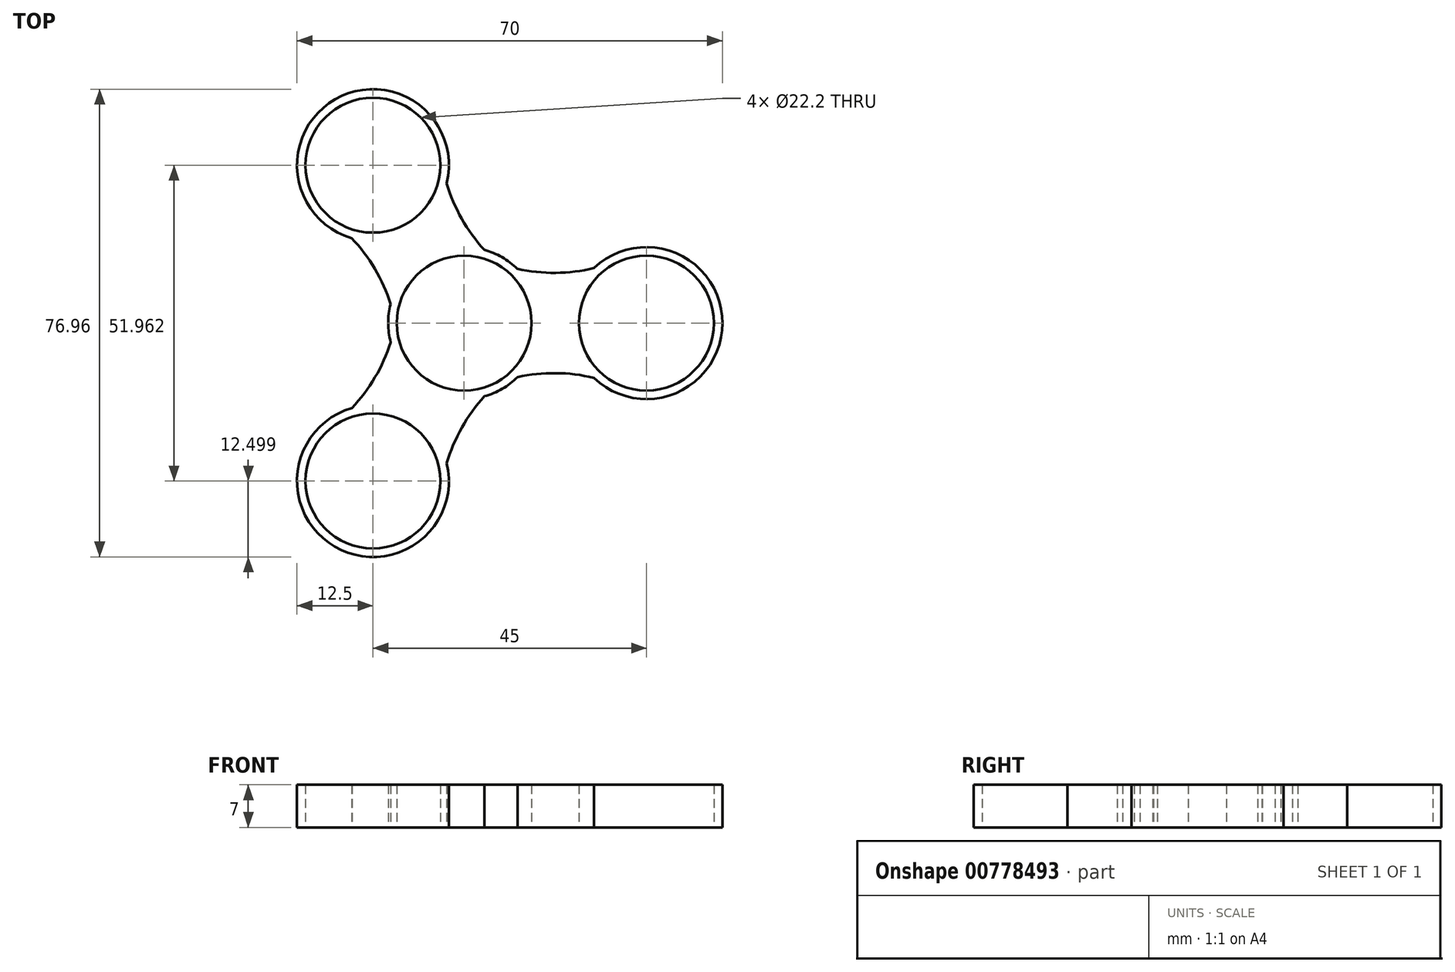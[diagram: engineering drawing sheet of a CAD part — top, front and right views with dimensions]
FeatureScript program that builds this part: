
annotation { "Feature Type Name" : "Feature", "Feature Type Description" : "" }
export const myFeature = defineFeature(function(context is Context, id is Id, definition is map)
    precondition{}
    {
        {
            var Q0;
            Q0=qCreatedBy(makeId("Top.planeOp"),FACE);
            var sketch = newSketch(context, id + "F0", { "sketchPlane" : qUnion([Q0])});
            skCircle(sketch, "E0", {"center": v(0, 0) * mm, "radius": 11.1 * mm});
            skCircle(sketch, "E1", {"center": v(0, 0) * mm, "radius": 12.5 * mm});
            skLineSegment(sketch, "E2", {"start": v(17.5, 0) * mm, "end": v(18.9, 0) * mm});
            skCircle(sketch, "E3", {"center": v(30, 0) * mm, "radius": 12.5 * mm});
            skCircle(sketch, "E4", {"center": v(30, 0) * mm, "radius": 11.1 * mm});
            skArc(sketch, "E5", {"start": v(21.34, -9.01) * mm, "mid": v(15.07, -8.24) * mm, "end": v(8.78, -8.9) * mm});
            skArc(sketch, "E6", {"start": v(8.75, 8.93) * mm, "mid": v(15.07, 8.27) * mm, "end": v(21.37, 9.05) * mm});
            skPoint(sketch, "E7.orphan", {"position": v(29.6, -12.5) * mm});
            skPoint(sketch, "E8.orphan", {"position": v(0, -12.5) * mm});
            skPoint(sketch, "E9.orphan", {"position": v(0, 12.5) * mm});
            skPoint(sketch, "E10.orphan", {"position": v(29.6, 12.5) * mm});
            skCircle(sketch, "E11.1.0", {"center": v(-15, 25.98) * mm, "radius": 12.5 * mm});
            skCircle(sketch, "E11.1.1", {"center": v(-15, 25.98) * mm, "radius": 11.1 * mm});
            skArc(sketch, "E11.1.2", {"start": v(-12.1, 3.1) * mm, "mid": v(-14.7, 8.91) * mm, "end": v(-18.52, 13.99) * mm});
            skArc(sketch, "E11.1.3", {"start": v(-2.86, 22.99) * mm, "mid": v(-0.4, 17.17) * mm, "end": v(3.31, 12.05) * mm});
            skCircle(sketch, "E11.2.0", {"center": v(-15, -25.98) * mm, "radius": 12.5 * mm});
            skCircle(sketch, "E11.2.1", {"center": v(-15, -25.98) * mm, "radius": 11.1 * mm});
            skArc(sketch, "E11.2.2", {"start": v(3.36, -12.04) * mm, "mid": v(-0.37, -17.18) * mm, "end": v(-2.85, -23.03) * mm});
            skArc(sketch, "E11.2.3", {"start": v(-18.47, -13.97) * mm, "mid": v(-14.67, -8.93) * mm, "end": v(-12.1, -3.16) * mm});
            skPoint(sketch, "E12.start.orphan", {"position": v(12.5, 0) * mm});
            skSolve(sketch);
        }
        {
            var Q0;
            Q0 = qSketchRegion(id + "F0", true);
            extrude(context, id + "F1", {"entities" : qUnion([Q0]), "depth" : 7 * mm, "offsetDistance" : 25.4 * mm});
        }
    });
